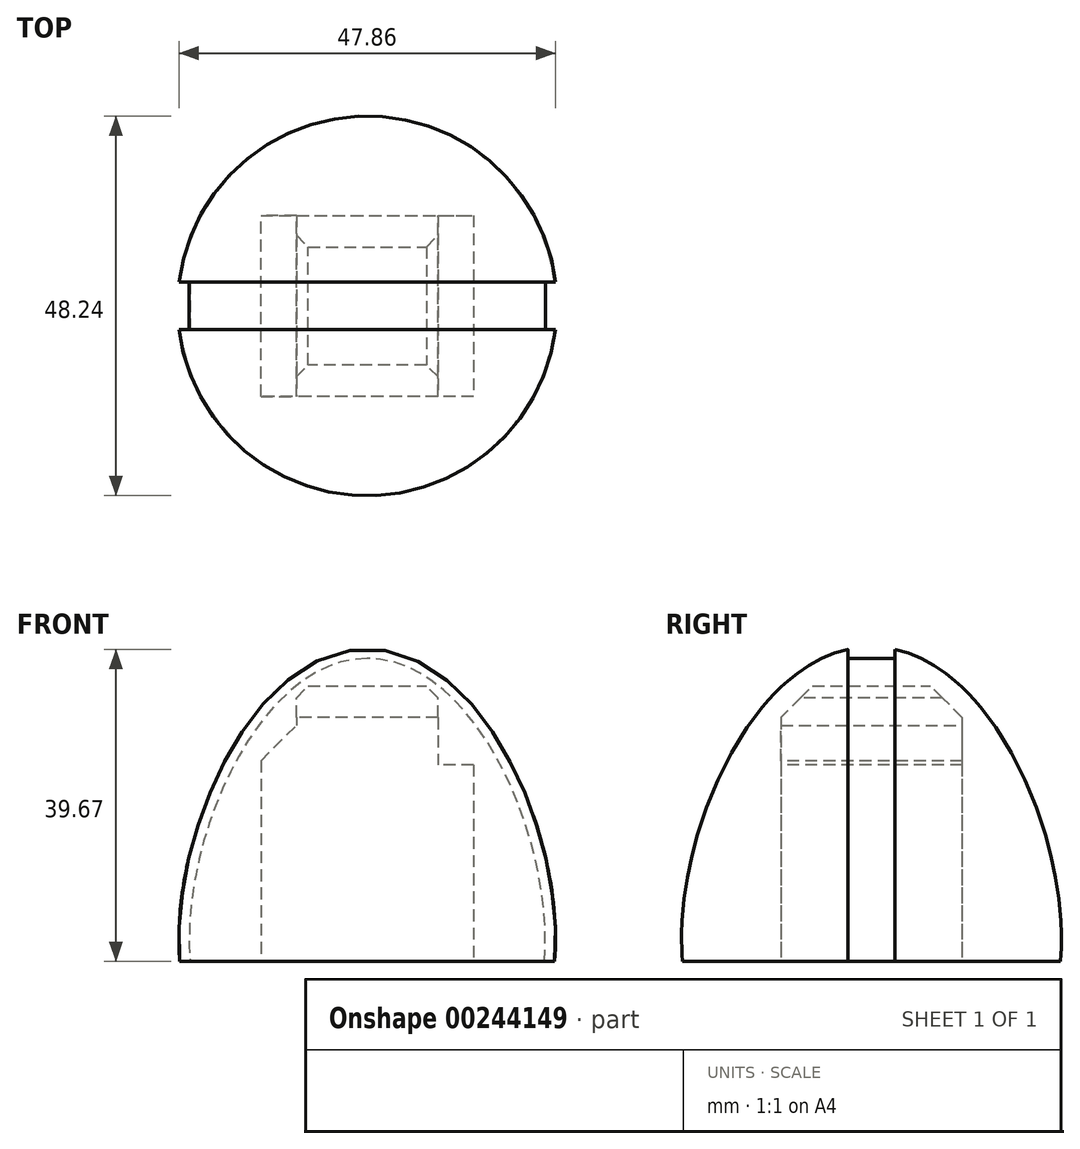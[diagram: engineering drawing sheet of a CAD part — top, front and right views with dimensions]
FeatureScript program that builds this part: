
annotation { "Feature Type Name" : "Feature", "Feature Type Description" : "" }
export const myFeature = defineFeature(function(context is Context, id is Id, definition is map)
    precondition{}
    {
        {
            var Q0;
            Q0=qCreatedBy(makeId("Front.planeOp"),FACE);
            var sketch = newSketch(context, id + "F0", { "sketchPlane" : qUnion([Q0])});
            skLineSegment(sketch, "E0", {"start": v(0, 0) * mm, "end": v(0, 60) * mm});
            skLineSegment(sketch, "E1", {"start": v(0, 0) * mm, "end": v(0, 20) * mm, "construction": true});
            skLineSegment(sketch, "E2", {"start": v(0, 20) * mm, "end": v(24, 20) * mm});
            skLineSegment(sketch, "E3", {"start": v(0, 60) * mm, "end": v(15, 60) * mm, "construction": true});
            skLineSegment(sketch, "E4", {"start": v(0, 0) * mm, "end": v(14, 0) * mm, "construction": true});
            skFitSpline(sketch, "E5", {"points": [v(0, 0) * mm, v(24, 20) * mm, v(0, 60) * mm], "startDerivative": vector(93.32, 0) * mm, "endDerivative": vector(-81.83, 0) * mm});
            skFitSpline(sketch, "E6.MirrorCS", {"points": [v(0, 0) * mm, v(-24, 20) * mm, v(0, 60) * mm], "startDerivative": vector(-93.32, 0) * mm, "endDerivative": vector(81.83, 0) * mm});
            skSolve(sketch);
        }
        {
            var Q0;
            {var subQ3=sQuery(id+"F0.wireOp",EDGE,"E2");Q0=makeQuery(id+"F0.imprint","IMPRINT",FACE,{"disambiguationData":[TD([[makeQuery(id+"F0.imprint","IMPRINT",EDGE,{"derivedFrom":subQ3}),1.0]])]});}
            var Q1;
            Q1=sQuery(id+"F0.wireOp",EDGE,"E0");
            revolve(context, id + "F1", {"entities" : qUnion([Q0]), "axis" : qUnion([Q1]), "revolveType" : RevolveType.FULL});
        }
        {
            var Q0;
            Q0=makeQuery(id+"F1.opRevolve","SWEPT_FACE",FACE,{"disambiguationData":[OSD([sQuery(id+"F0.wireOp",EDGE,"E2")])]});
            var sketch = newSketch(context, id + "F2", { "sketchPlane" : qUnion([Q0])});
            skLineSegment(sketch, "E7", {"start": v(0, 0) * mm, "end": v(13.5, 0) * mm});
            skLineSegment(sketch, "E8", {"start": v(13.5, 0) * mm, "end": v(13.5, 11.5) * mm});
            skLineSegment(sketch, "E9", {"start": v(13.5, 11.5) * mm, "end": v(-13.5, 11.5) * mm});
            skLineSegment(sketch, "E10", {"start": v(-13.5, 11.5) * mm, "end": v(-13.5, -11.5) * mm});
            skLineSegment(sketch, "E11", {"start": v(-13.5, -11.5) * mm, "end": v(13.5, -11.5) * mm});
            skLineSegment(sketch, "E12", {"start": v(13.5, -11.5) * mm, "end": v(13.5, 0) * mm});
            skSolve(sketch);
        }
        {
            var Q0;
            Q0 = qSketchRegion(id + "F2", true);
            extrude(context, id + "F3", {"entities" : qUnion([Q0]), "operationType" : NewBodyOperationType.REMOVE, "oppositeDirection" : true, "depth" : 25 * mm});
        }
        {
            var Q0;
            Q0=makeQuery(id+"F3.boolean.opBoolean","COPY",FACE,{"derivedFrom":makeQuery(id+"F3.opExtrude","CAP_FACE",FACE,{"disambiguationData":[OSD([sQuery(id+"F2.wireOp",EDGE,"E8"),sQuery(id+"F2.wireOp",EDGE,"E9"),sQuery(id+"F2.wireOp",EDGE,"E10"),sQuery(id+"F2.wireOp",EDGE,"E11"),sQuery(id+"F2.wireOp",EDGE,"E12")])],"isStart":false})});
            var sketch = newSketch(context, id + "F4", { "sketchPlane" : qUnion([Q0])});
            skLineSegment(sketch, "E13", {"start": v(0, 0) * mm, "end": v(5, 0) * mm, "construction": true});
            skLineSegment(sketch, "E14", {"start": v(5, 0) * mm, "end": v(5, 5) * mm});
            skLineSegment(sketch, "E15", {"start": v(5, 5) * mm, "end": v(-5, 5) * mm});
            skLineSegment(sketch, "E16", {"start": v(-5, 5) * mm, "end": v(-5, -5) * mm});
            skLineSegment(sketch, "E17", {"start": v(-5, -5) * mm, "end": v(5, -5) * mm});
            skLineSegment(sketch, "E18", {"start": v(5, -5) * mm, "end": v(5, 0) * mm});
            skSolve(sketch);
        }
        {
            var Q0;
            Q0 = qSketchRegion(id + "F4", true);
            extrude(context, id + "F5", {"entities" : qUnion([Q0]), "operationType" : NewBodyOperationType.REMOVE, "oppositeDirection" : true, "depth" : 10 * mm});
        }
        {
            var Q0;
            Q0=makeQuery(id+"F3.boolean.opBoolean","COPY",FACE,{"derivedFrom":makeQuery(id+"F3.opExtrude","CAP_FACE",FACE,{"disambiguationData":[OSD([sQuery(id+"F2.wireOp",EDGE,"E8"),sQuery(id+"F2.wireOp",EDGE,"E9"),sQuery(id+"F2.wireOp",EDGE,"E10"),sQuery(id+"F2.wireOp",EDGE,"E11"),sQuery(id+"F2.wireOp",EDGE,"E12")])],"isStart":false})});
            var sketch = newSketch(context, id + "F6", { "sketchPlane" : qUnion([Q0])});
            skLineSegment(sketch, "E19", {"start": v(0, 0) * mm, "end": v(9, 0) * mm, "construction": true});
            skLineSegment(sketch, "E20", {"start": v(9, 0) * mm, "end": v(9, 11.5) * mm});
            skLineSegment(sketch, "E21", {"start": v(9, 11.5) * mm, "end": v(-9, 11.5) * mm});
            skLineSegment(sketch, "E22", {"start": v(-9, 11.5) * mm, "end": v(-9, -11.5) * mm});
            skLineSegment(sketch, "E23", {"start": v(-9, -11.5) * mm, "end": v(9, -11.5) * mm});
            skLineSegment(sketch, "E24", {"start": v(9, -11.5) * mm, "end": v(9, 0) * mm});
            skSolve(sketch);
        }
        {
            var Q0;
            Q0 = qSketchRegion(id + "F6", true);
            extrude(context, id + "F7", {"entities" : qUnion([Q0]), "operationType" : NewBodyOperationType.REMOVE, "oppositeDirection" : true, "depth" : 6 * mm});
        }
        {
            var Q0;
            Q0=makeQuery(id+"F7.boolean.opBoolean","COPY",EDGE,{"derivedFrom":makeQuery(id+"F7.opExtrude","CAP_EDGE",EDGE,{"disambiguationData":[OSD([sQuery(id+"F6.wireOp",EDGE,"E22")])],"isStart":true})});
            var Q1;
            Q1=makeQuery(id+"F7.boolean.opBoolean","COPY",EDGE,{"derivedFrom":makeQuery(id+"F7.opExtrude","CAP_EDGE",EDGE,{"disambiguationData":[OSD([sQuery(id+"F6.wireOp",EDGE,"E20"),sQuery(id+"F6.wireOp",EDGE,"E24")])],"isStart":true})});
            chamfer(context, id + "F8", {"entities" : qUnion([Q0, Q1]), "width" : 5 * mm, "tangentPropagation" : true});
        }
        {
            var Q0;
            Q0=makeQuery(id+"F7.boolean.opBoolean","INTERSECT",EDGE,{"derivedFrom":[makeQuery(id+"F5.boolean.opBoolean","COPY",FACE,{"derivedFrom":makeQuery(id+"F5.opExtrude","SWEPT_FACE",FACE,{"disambiguationData":[OSD([sQuery(id+"F4.wireOp",EDGE,"E16")])]})}),makeQuery(id+"F7.opExtrude","CAP_FACE",FACE,{"disambiguationData":[OSD([sQuery(id+"F6.wireOp",EDGE,"E20"),sQuery(id+"F6.wireOp",EDGE,"E21"),sQuery(id+"F6.wireOp",EDGE,"E22"),sQuery(id+"F6.wireOp",EDGE,"E23"),sQuery(id+"F6.wireOp",EDGE,"E24")])],"isStart":false})]});
            var Q1;
            Q1=makeQuery(id+"F7.boolean.opBoolean","INTERSECT",EDGE,{"derivedFrom":[makeQuery(id+"F5.boolean.opBoolean","COPY",FACE,{"derivedFrom":makeQuery(id+"F5.opExtrude","SWEPT_FACE",FACE,{"disambiguationData":[OSD([sQuery(id+"F4.wireOp",EDGE,"E15")])]})}),makeQuery(id+"F7.opExtrude","CAP_FACE",FACE,{"disambiguationData":[OSD([sQuery(id+"F6.wireOp",EDGE,"E20"),sQuery(id+"F6.wireOp",EDGE,"E21"),sQuery(id+"F6.wireOp",EDGE,"E22"),sQuery(id+"F6.wireOp",EDGE,"E23"),sQuery(id+"F6.wireOp",EDGE,"E24")])],"isStart":false})]});
            var Q2;
            Q2=makeQuery(id+"F7.boolean.opBoolean","INTERSECT",EDGE,{"derivedFrom":[makeQuery(id+"F5.boolean.opBoolean","COPY",FACE,{"derivedFrom":makeQuery(id+"F5.opExtrude","SWEPT_FACE",FACE,{"disambiguationData":[OSD([sQuery(id+"F4.wireOp",EDGE,"E14"),sQuery(id+"F4.wireOp",EDGE,"E18")])]})}),makeQuery(id+"F7.opExtrude","CAP_FACE",FACE,{"disambiguationData":[OSD([sQuery(id+"F6.wireOp",EDGE,"E20"),sQuery(id+"F6.wireOp",EDGE,"E21"),sQuery(id+"F6.wireOp",EDGE,"E22"),sQuery(id+"F6.wireOp",EDGE,"E23"),sQuery(id+"F6.wireOp",EDGE,"E24")])],"isStart":false})]});
            var Q3;
            Q3=makeQuery(id+"F7.boolean.opBoolean","INTERSECT",EDGE,{"derivedFrom":[makeQuery(id+"F5.boolean.opBoolean","COPY",FACE,{"derivedFrom":makeQuery(id+"F5.opExtrude","SWEPT_FACE",FACE,{"disambiguationData":[OSD([sQuery(id+"F4.wireOp",EDGE,"E17")])]})}),makeQuery(id+"F7.opExtrude","CAP_FACE",FACE,{"disambiguationData":[OSD([sQuery(id+"F6.wireOp",EDGE,"E20"),sQuery(id+"F6.wireOp",EDGE,"E21"),sQuery(id+"F6.wireOp",EDGE,"E22"),sQuery(id+"F6.wireOp",EDGE,"E23"),sQuery(id+"F6.wireOp",EDGE,"E24")])],"isStart":false})]});
            chamfer(context, id + "F9", {"entities" : qUnion([Q0, Q1, Q2, Q3]), "width" : 6.5 * mm, "tangentPropagation" : true});
        }
        {
            var Q0;
            Q0=qCreatedBy(makeId("Right.planeOp"),FACE);
            var sketch = newSketch(context, id + "F10", { "sketchPlane" : qUnion([Q0])});
            skLineSegment(sketch, "E25", {"start": v(0, 0) * mm, "end": v(3, 0) * mm});
            skLineSegment(sketch, "E26", {"start": v(3, 0) * mm, "end": v(3, 1.5) * mm});
            skLineSegment(sketch, "E27", {"start": v(3, 1.5) * mm, "end": v(-3, 1.5) * mm});
            skLineSegment(sketch, "E28", {"start": v(-3, 1.5) * mm, "end": v(-3, 0) * mm});
            skLineSegment(sketch, "E29", {"start": v(-3, 0) * mm, "end": v(0, 0) * mm});
            skSolve(sketch);
        }
        {
            var Q0;
            Q0=makeQuery(id+"F10.imprint","IMPRINT",FACE,{"disambiguationData":[TD([[makeQuery(id+"F10.imprint","IMPRINT",EDGE,{"derivedFrom":sQuery(id+"F10.wireOp",EDGE,"E25")}),1.0]])]});
            var Q1;
            Q1=sQuery(id+"F0.wireOp",EDGE,"E5");
            var Q2;
            Q2=sQuery(id+"F0.wireOp",EDGE,"E6.MirrorCS");
            sweep(context, id + "F11", {"operationType" : NewBodyOperationType.REMOVE, "profiles" : qUnion([Q0]), "path" : qUnion([Q1, Q2])});
        }
    });
